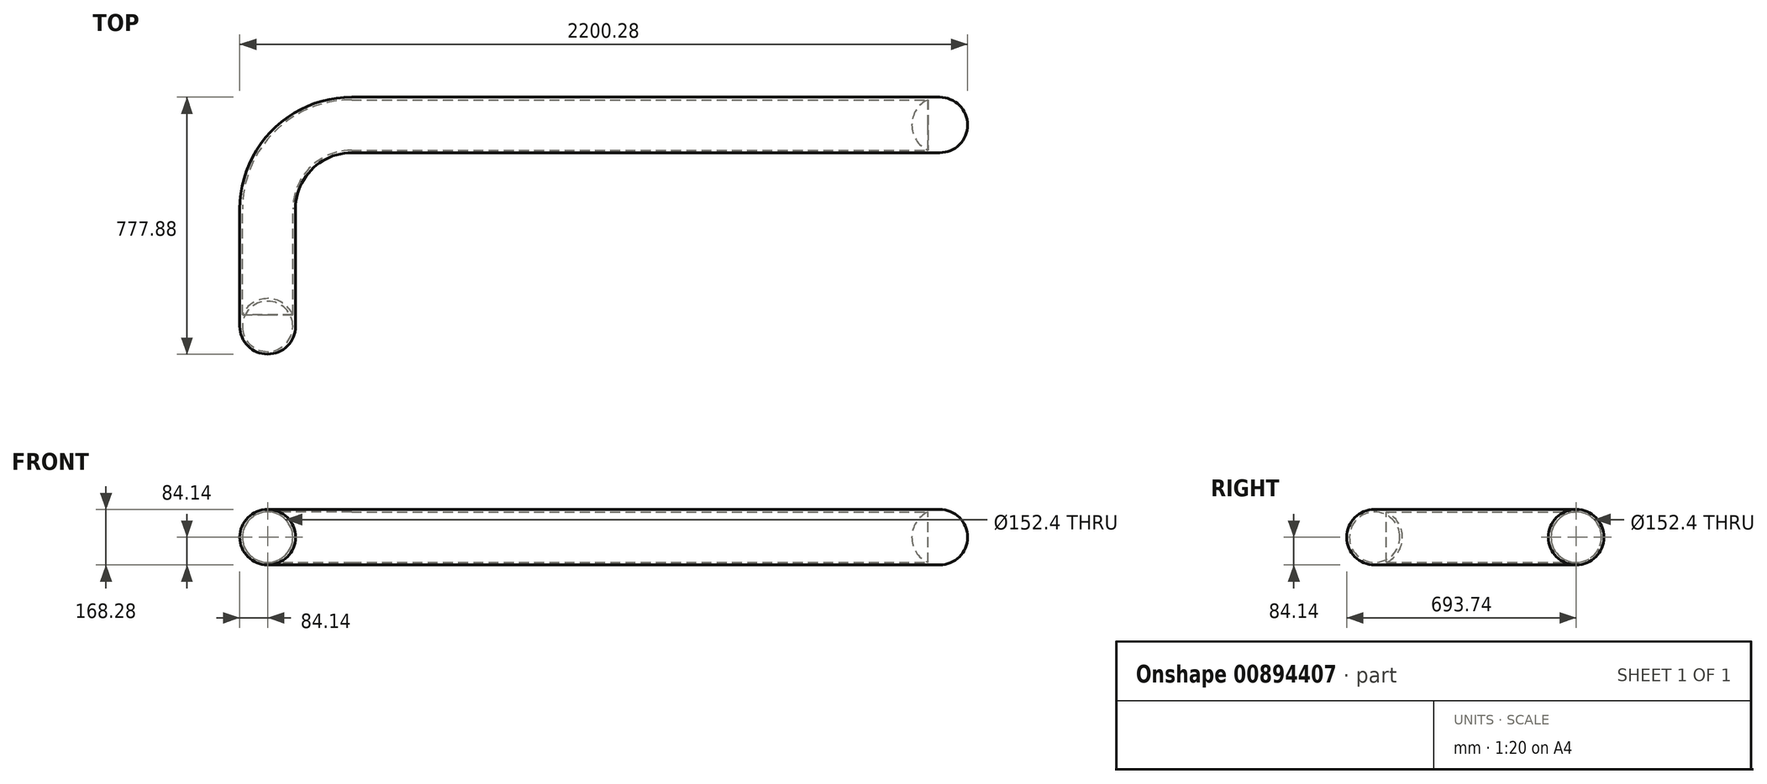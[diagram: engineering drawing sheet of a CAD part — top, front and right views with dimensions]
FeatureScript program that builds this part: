
annotation { "Feature Type Name" : "Feature", "Feature Type Description" : "" }
export const myFeature = defineFeature(function(context is Context, id is Id, definition is map)
    precondition{}
    {
        {
            var Q0;
            Q0=qCreatedBy(makeId("Top.planeOp"),FACE);
            var sketch = newSketch(context, id + "F0", { "sketchPlane" : qUnion([Q0])});
            skLineSegment(sketch, "E0", {"start": v(0, 0) * mm, "end": v(0, 355.6) * mm});
            skLineSegment(sketch, "E1", {"start": v(254, 609.6) * mm, "end": v(2032, 609.6) * mm});
            skArc(sketch, "E2", {"start": v(254, 609.6) * mm, "mid": v(74.4, 535.2) * mm, "end": v(0, 355.6) * mm});
            skSolve(sketch);
        }
        {
            var Q0;
            Q0=qCreatedBy(makeId("Front.planeOp"),FACE);
            var sketch = newSketch(context, id + "F1", { "sketchPlane" : qUnion([Q0])});
            skCircle(sketch, "E3", {"center": v(0, 0) * mm, "radius": 84.14 * mm});
            skCircle(sketch, "E4", {"center": v(0, 0) * mm, "radius": 76.2 * mm});
            skSolve(sketch);
        }
        {
            var Q0;
            Q0=makeQuery(id+"F1.imprint","IMPRINT",FACE,{"disambiguationData":[TD([[makeQuery(id+"F1.imprint","IMPRINT",EDGE,{"derivedFrom":sQuery(id+"F1.wireOp",EDGE,"E3")}),1.0]])]});
            var Q1;
            Q1=sQuery(id+"F0.wireOp",EDGE,"E0");
            var Q2;
            Q2=sQuery(id+"F0.wireOp",EDGE,"E2");
            var Q3;
            Q3=sQuery(id+"F0.wireOp",EDGE,"E1");
            sweep(context, id + "F2", {"profiles" : qUnion([Q0]), "path" : qUnion([Q1, Q2, Q3])});
        }
        {
            var Q0;
            Q0=qCreatedBy(makeId("Top.planeOp"),FACE);
            var sketch = newSketch(context, id + "F3", { "sketchPlane" : qUnion([Q0])});
            skArc(sketch, "E5", {"start": v(-84.14, 0) * mm, "mid": v(0, -84.14) * mm, "end": v(84.14, 0) * mm});
            skArc(sketch, "E6", {"start": v(-76.2, 0) * mm, "mid": v(0, -76.2) * mm, "end": v(76.2, 0) * mm});
            skLineSegment(sketch, "E7", {"start": v(-84.14, 0) * mm, "end": v(84.14, 0) * mm});
            skLineSegment(sketch, "E8", {"start": v(0, -39.78) * mm, "end": v(0, 49.76) * mm});
            skSolve(sketch);
        }
        {
            var Q0;
            {var subQ0=sQuery(id+"F3.wireOp",EDGE,"E5");Q0=makeQuery(id+"F3.imprint","IMPRINT",FACE,{"disambiguationData":[TD([[makeQuery(id+"F3.imprint","IMPRINT",EDGE,{"derivedFrom":subQ0}),1.0]])]});}
            var Q1;
            Q1=sQuery(id+"F3.wireOp",EDGE,"E7");
            revolve(context, id + "F4", {"operationType" : NewBodyOperationType.ADD, "surfaceOperationType" : NewSurfaceOperationType.NEW, "entities" : qUnion([Q0]), "axis" : qUnion([Q1]), "revolveType" : RevolveType.TWO_DIRECTIONS, "angle" : 180 * degree, "angleBack" : 180 * degree});
        }
        {
            var Q0;
            Q0=makeQuery(id+"F2.opSweep","CAP_FACE",FACE,{"disambiguationData":[OSD([sQuery(id+"F0.wireOp",VERTEX,"E1.end"),sQuery(id+"F1.wireOp",EDGE,"E3"),sQuery(id+"F1.wireOp",EDGE,"E4")])],"isStart":false});
            var sketch = newSketch(context, id + "F5", { "sketchPlane" : qUnion([Q0])});
            skLineSegment(sketch, "E9", {"start": v(609.6, 0) * mm, "end": v(484.99, 0) * mm});
            skLineSegment(sketch, "E10", {"start": v(484.99, 0) * mm, "end": v(766.7, 0) * mm});
            skArc(sketch, "E11", {"start": v(685.8, 0) * mm, "mid": v(609.6, 76.2) * mm, "end": v(533.4, 0) * mm});
            skArc(sketch, "E12", {"start": v(693.74, 0) * mm, "mid": v(609.6, 84.14) * mm, "end": v(525.46, 0) * mm});
            skSolve(sketch);
        }
        {
            var Q0;
            Q0 = qSketchRegion(id + "F5", true);
            var Q1;
            Q1=sQuery(id+"F5.wireOp",EDGE,"E10");
            revolve(context, id + "F6", {"operationType" : NewBodyOperationType.ADD, "surfaceOperationType" : NewSurfaceOperationType.NEW, "entities" : qUnion([Q0]), "axis" : qUnion([Q1]), "revolveType" : RevolveType.FULL});
        }
    });
